# Revit family: Plumbing_Pipes_Johnson-Suisse_Bottle_Trap
name_source: partatom
category: Plumbing Fixtures
revit_build: Autodesk Revit 2015 (Build: 20140606_1530(x64)
units: mm (PartAtom-declared; Revit-internal decimal feet)

## types (1)
- Bottle Trap
    BIMobject category = Pipes
    Brand url = http://www.johnsonsuisse.com.au
    Design country = Spain
    EAN code = https://9322798021427
    Edition number = 1
    IFC Classification = Pipe Fitting
    Manufacturer country = China
    Manufacturer name = Johnson Suisse
    Material main = Chrome
    Material secondary = Chrome
    NBS Reference Code = 50-24-77
    NBS Reference Description = Sanitary Appliance Traps
    Nominal height = 300 mm  [stored 0.984252 ft]
    Nominal width = 38 mm  [stored 0.124672 ft]
    Product Guid = af022356-e152-4752-b442-916407de6dc7
    Product SKU = BT1
    Product data url = https://bimobject.com
    Product family = Basins
    Product group = Components
    Product url = https://johnsonsuisse.com.au
    QR code = http://bimobject.com
    Technical description = https://johnsonsuisse.com.au
    Type = bottle_trap : Default
    UNSPSC Code = 3018
    Uniclass 1.4 Code = L7254
    Uniclass 1.4 Description = Traps for sinks and basins
    Uniclass 2.0 Code = PR-50-24-77
    Uniclass 2.0 Description = Sanitary Appliance Traps
    Weight Net (Kg) = 1.33

note: [stored X ft] marks values corroborated as IEEE doubles in the binary element streams (Revit-internal decimal feet)

## geometry (parser evidence)
native form markers: Sweep x5
no freeform markers — native parametric forms only
